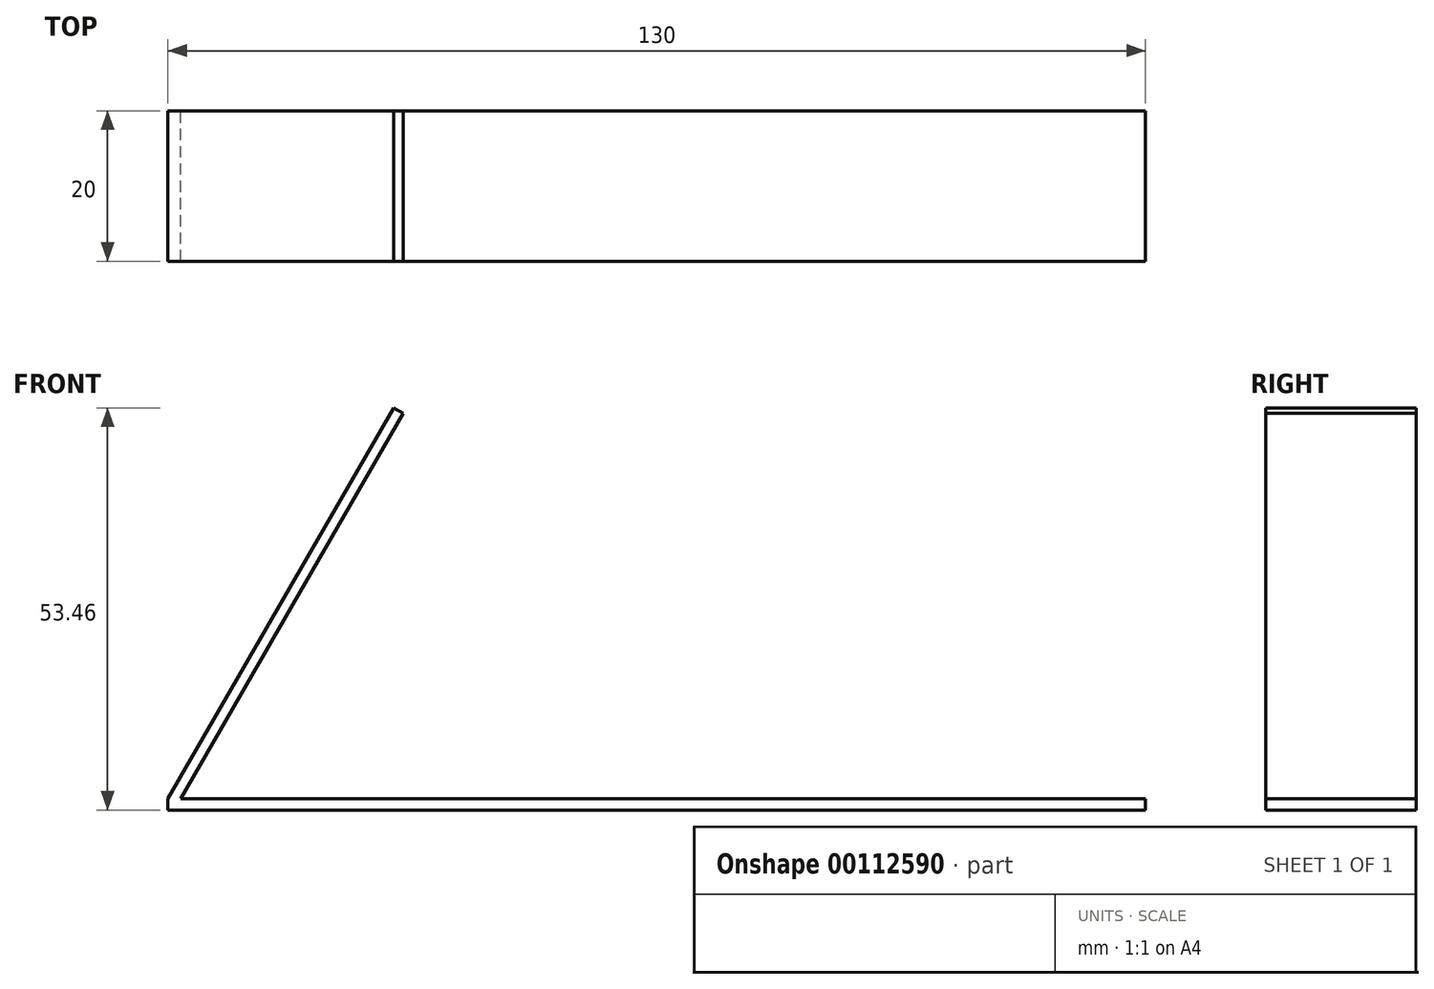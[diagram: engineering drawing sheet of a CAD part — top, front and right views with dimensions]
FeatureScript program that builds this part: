
annotation { "Feature Type Name" : "Feature", "Feature Type Description" : "" }
export const myFeature = defineFeature(function(context is Context, id is Id, definition is map)
    precondition{}
    {
        {
            var Q0;
            Q0=qCreatedBy(makeId("Front.planeOp"),FACE);
            var sketch = newSketch(context, id + "F0", { "sketchPlane" : qUnion([Q0])});
            skLineSegment(sketch, "E0.bottom", {"start": v(0, 0) * mm, "end": v(130, 0) * mm});
            skLineSegment(sketch, "E0.top", {"start": v(0, 1.5) * mm, "end": v(130, 1.5) * mm});
            skLineSegment(sketch, "E0.left", {"start": v(0, 0) * mm, "end": v(0, 1.5) * mm});
            skLineSegment(sketch, "E0.right", {"start": v(130, 0) * mm, "end": v(130, 1.5) * mm});
            skSolve(sketch);
        }
        {
            var Q0;
            Q0 = qSketchRegion(id + "F0", true);
            extrude(context, id + "F1", {"entities" : qUnion([Q0]), "endBound" : BoundingType.SYMMETRIC, "depth" : 20 * mm});
        }
        {
            var Q0;
            Q0=makeQuery(id+"F1.opExtrude","SWEPT_EDGE",EDGE,{"disambiguationData":[OSD([sQuery(id+"F0.wireOp",EDGE,"E0.top"),sQuery(id+"F0.wireOp",EDGE,"E0.left")])]});
            cPlane(context, id + "F2", {"entities" : qUnion([Q0]), "cplaneType" : CPlaneType.LINE_ANGLE, "offset" : 25 * mm, "angle" : 120 * degree, "width" : 150 * mm, "height" : 150 * mm});
        }
        {
            var Q0;
            Q0=qCreatedBy(id+"F2.planeOp",FACE);
            var sketch = newSketch(context, id + "F3", { "sketchPlane" : qUnion([Q0])});
            skLineSegment(sketch, "E1.0", {"start": v(-10, 1.3) * mm, "end": v(10, 1.3) * mm});
            skLineSegment(sketch, "E2", {"start": v(-10, 1.3) * mm, "end": v(-10, 61.3) * mm});
            skLineSegment(sketch, "E3", {"start": v(-10, 61.3) * mm, "end": v(10, 61.3) * mm});
            skLineSegment(sketch, "E4", {"start": v(10, 61.3) * mm, "end": v(10, 1.3) * mm});
            skSolve(sketch);
        }
        {
            var Q0;
            Q0 = qSketchRegion(id + "F3", true);
            extrude(context, id + "F4", {"entities" : qUnion([Q0]), "operationType" : NewBodyOperationType.ADD, "depth" : 1.5 * mm});
        }
    });
